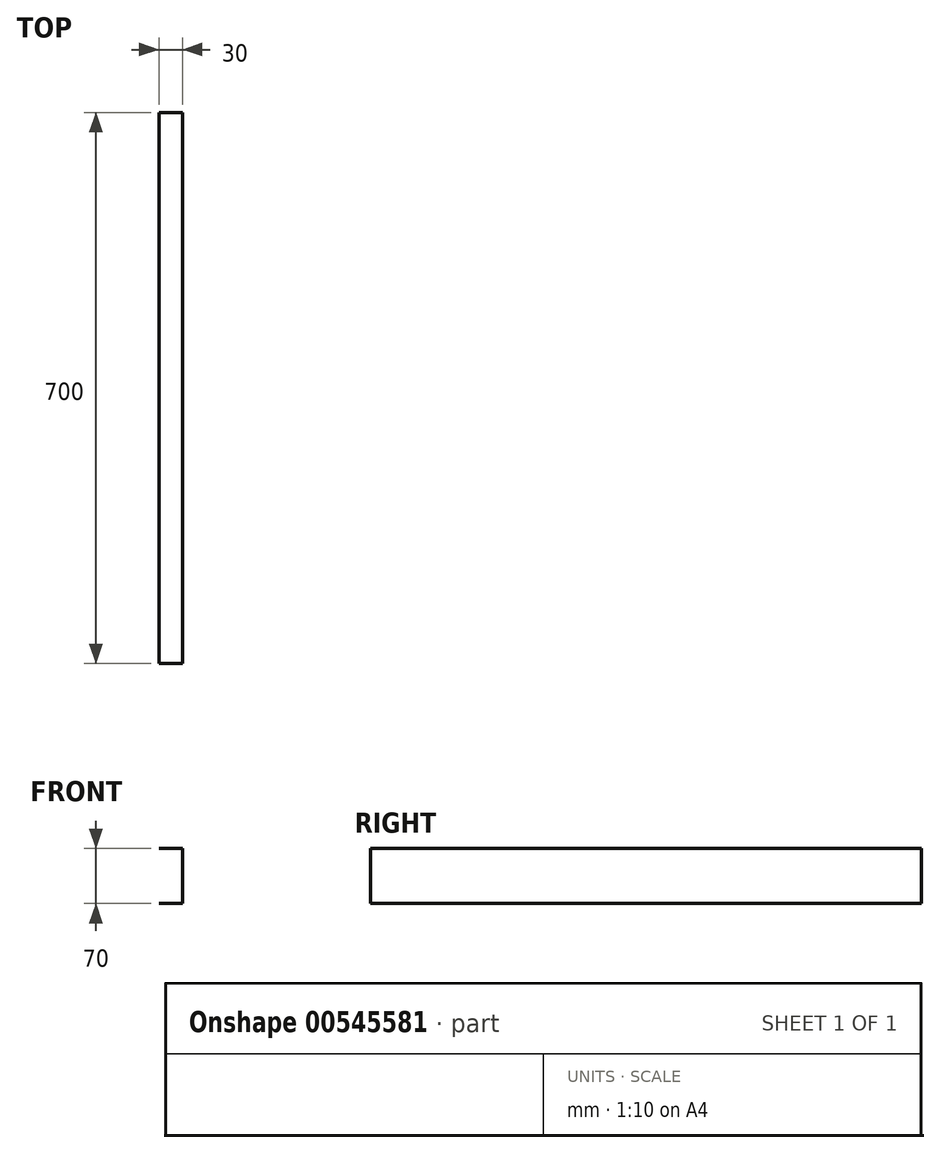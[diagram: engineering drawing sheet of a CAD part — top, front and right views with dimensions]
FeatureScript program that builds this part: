
annotation { "Feature Type Name" : "Feature", "Feature Type Description" : "" }
export const myFeature = defineFeature(function(context is Context, id is Id, definition is map)
    precondition{}
    {
        {
            var Q0;
            Q0=qCreatedBy(makeId("Front.planeOp"),FACE);
            var sketch = newSketch(context, id + "F0", { "sketchPlane" : qUnion([Q0])});
            skLineSegment(sketch, "E0", {"start": v(-9, -63.8) * mm, "end": v(21, -63.8) * mm});
            skLineSegment(sketch, "E1", {"start": v(21, -63.8) * mm, "end": v(21, 6.2) * mm});
            skLineSegment(sketch, "E2", {"start": v(21, 6.2) * mm, "end": v(-9, 6.2) * mm});
            skSolve(sketch);
        }
        {
            var Q0;
            Q0=sQuery(id+"F0.wireOp",EDGE,"E2");
            var Q1;
            Q1=sQuery(id+"F0.wireOp",EDGE,"E1");
            var Q2;
            Q2=sQuery(id+"F0.wireOp",EDGE,"E0");
            extrude(context, id + "F1", {"bodyType" : ToolBodyType.SURFACE, "surfaceEntities" : qUnion([Q0, Q1, Q2]), "oppositeDirection" : true, "depth" : 700 * mm, "offsetDistance" : 25 * mm});
        }
    });
